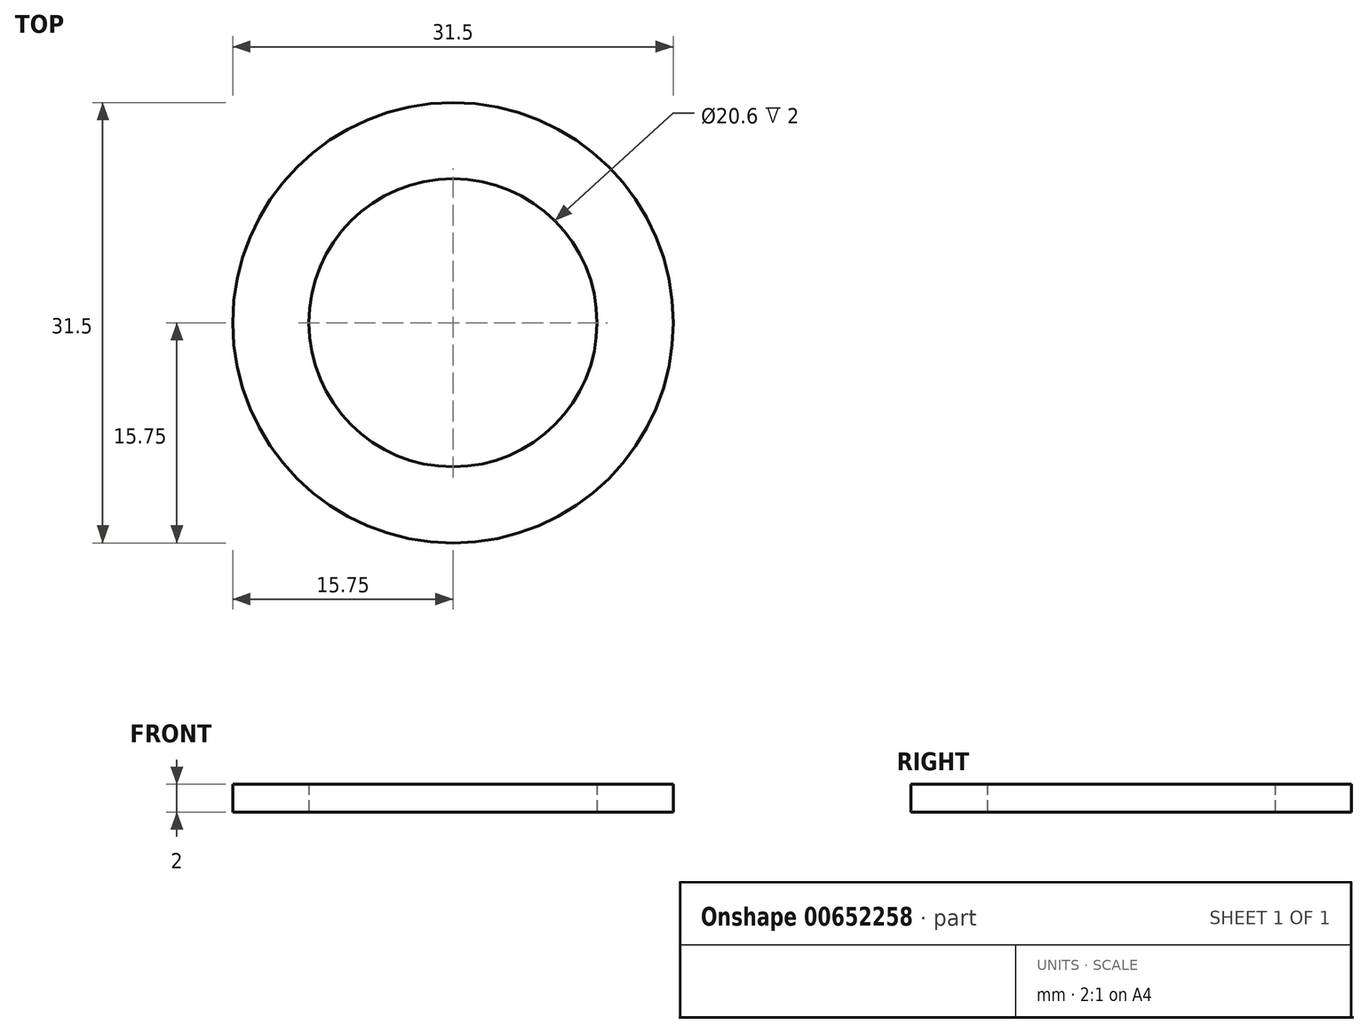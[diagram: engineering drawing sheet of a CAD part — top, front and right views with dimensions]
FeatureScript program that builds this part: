
annotation { "Feature Type Name" : "Feature", "Feature Type Description" : "" }
export const myFeature = defineFeature(function(context is Context, id is Id, definition is map)
    precondition{}
    {
        {
            var Q0;
            Q0=qCreatedBy(makeId("Top.planeOp"),FACE);
            var sketch = newSketch(context, id + "F0", { "sketchPlane" : qUnion([Q0])});
            skCircle(sketch, "E0", {"center": v(0, 0) * mm, "radius": 15.75 * mm});
            skCircle(sketch, "E1", {"center": v(0, 0) * mm, "radius": 10.3 * mm});
            skSolve(sketch);
        }
        {
            var Q0;
            Q0=makeQuery(id+"F0.imprint","IMPRINT",FACE,{"disambiguationData":[TD([[makeQuery(id+"F0.imprint","IMPRINT",EDGE,{"derivedFrom":sQuery(id+"F0.wireOp",EDGE,"E0")}),1.0]])]});
            extrude(context, id + "F1", {"entities" : qUnion([Q0]), "depth" : 2 * mm, "offsetDistance" : 25 * mm});
        }
    });
